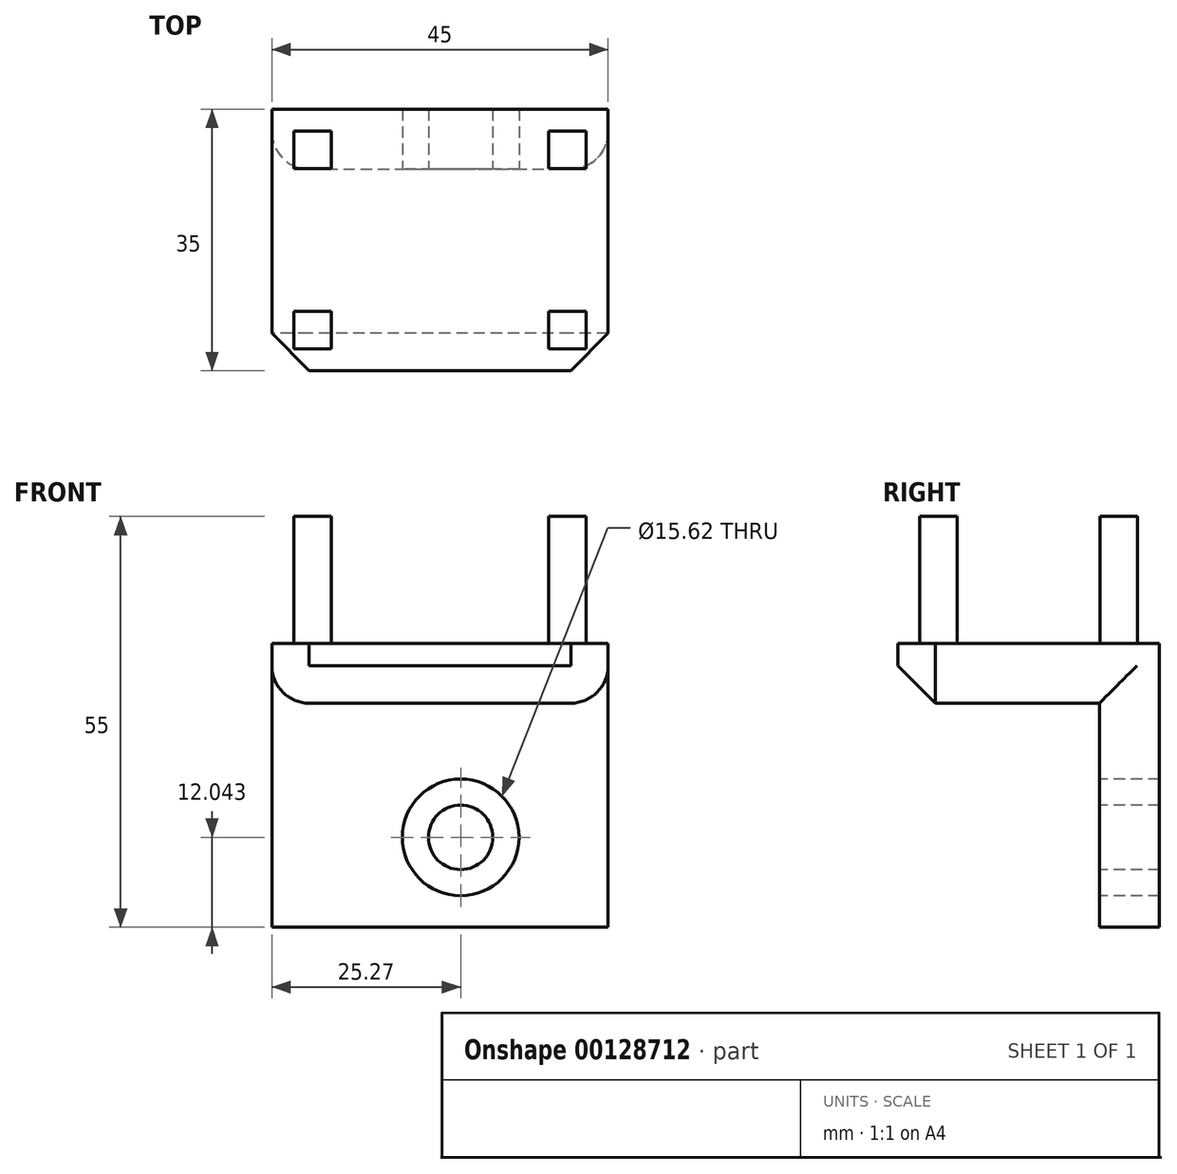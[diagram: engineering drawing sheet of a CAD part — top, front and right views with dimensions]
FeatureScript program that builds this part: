
annotation { "Feature Type Name" : "Feature", "Feature Type Description" : "" }
export const myFeature = defineFeature(function(context is Context, id is Id, definition is map)
    precondition{}
    {
        {
            var Q0;
            Q0=qCreatedBy(makeId("Top.planeOp"),FACE);
            var sketch = newSketch(context, id + "F0", { "sketchPlane" : qUnion([Q0])});
            skLineSegment(sketch, "E0.bottom", {"start": v(-22.5, -17.5) * mm, "end": v(22.5, -17.5) * mm});
            skLineSegment(sketch, "E0.top", {"start": v(-22.5, 17.5) * mm, "end": v(22.5, 17.5) * mm});
            skLineSegment(sketch, "E0.left", {"start": v(-22.5, -17.5) * mm, "end": v(-22.5, 17.5) * mm});
            skLineSegment(sketch, "E0.right", {"start": v(22.5, -17.5) * mm, "end": v(22.5, 17.5) * mm});
            skPoint(sketch, "E0.middle", {"position": v(0, 0) * mm});
            skLineSegment(sketch, "E1.top", {"start": v(-22.5, 9.49) * mm, "end": v(22.5, 9.49) * mm});
            skLineSegment(sketch, "E1.left", {"start": v(-22.5, 17.5) * mm, "end": v(-22.5, 9.49) * mm});
            skLineSegment(sketch, "E1.right", {"start": v(22.5, 17.5) * mm, "end": v(22.5, 9.49) * mm});
            skLineSegment(sketch, "E2.bottom", {"start": v(14.55, -9.55) * mm, "end": v(19.55, -9.55) * mm});
            skLineSegment(sketch, "E2.top", {"start": v(14.55, -14.55) * mm, "end": v(19.55, -14.55) * mm});
            skLineSegment(sketch, "E2.left", {"start": v(14.55, -9.55) * mm, "end": v(14.55, -14.55) * mm});
            skLineSegment(sketch, "E2.right", {"start": v(19.55, -9.55) * mm, "end": v(19.55, -14.55) * mm});
            skLineSegment(sketch, "E3.MirrorCS", {"start": v(19.55, 9.55) * mm, "end": v(19.55, 14.55) * mm});
            skLineSegment(sketch, "E4.MirrorCS", {"start": v(14.55, 9.55) * mm, "end": v(14.55, 14.55) * mm});
            skLineSegment(sketch, "E5.MirrorCS", {"start": v(14.55, 14.55) * mm, "end": v(19.55, 14.55) * mm});
            skLineSegment(sketch, "E6.MirrorCS", {"start": v(14.55, 9.55) * mm, "end": v(19.55, 9.55) * mm});
            skLineSegment(sketch, "E7.MirrorCS", {"start": v(-19.55, 9.55) * mm, "end": v(-19.55, 14.55) * mm});
            skLineSegment(sketch, "E8.MirrorCS", {"start": v(-19.55, -9.55) * mm, "end": v(-19.55, -14.55) * mm});
            skLineSegment(sketch, "E9.MirrorCS", {"start": v(-14.55, -9.55) * mm, "end": v(-14.55, -14.55) * mm});
            skLineSegment(sketch, "E10.MirrorCS", {"start": v(-14.55, -14.55) * mm, "end": v(-19.55, -14.55) * mm});
            skLineSegment(sketch, "E11.MirrorCS", {"start": v(-14.55, 9.55) * mm, "end": v(-14.55, 14.55) * mm});
            skLineSegment(sketch, "E12.MirrorCS", {"start": v(-14.55, -9.55) * mm, "end": v(-19.55, -9.55) * mm});
            skLineSegment(sketch, "E13.MirrorCS", {"start": v(-14.55, 9.55) * mm, "end": v(-19.55, 9.55) * mm});
            skLineSegment(sketch, "E14.MirrorCS", {"start": v(-14.55, 14.55) * mm, "end": v(-19.55, 14.55) * mm});
            skSolve(sketch);
        }
        {
            var Q0;
            Q0=makeQuery(id+"F0.imprint","IMPRINT",FACE,{"disambiguationData":[TD([[makeQuery(id+"F0.imprint","IMPRINT",EDGE,{"derivedFrom":sQuery(id+"F0.wireOp",EDGE,"E7.MirrorCS")}),-1.0]])]});
            var Q1;
            Q1=makeQuery(id+"F0.imprint","IMPRINT",FACE,{"disambiguationData":[TD([[makeQuery(id+"F0.imprint","IMPRINT",EDGE,{"derivedFrom":sQuery(id+"F0.wireOp",EDGE,"E8.MirrorCS")}),1.0]])]});
            var Q2;
            Q2=makeQuery(id+"F0.imprint","IMPRINT",FACE,{"disambiguationData":[TD([[makeQuery(id+"F0.imprint","IMPRINT",EDGE,{"derivedFrom":sQuery(id+"F0.wireOp",EDGE,"E2.bottom")}),-1.0]])]});
            var Q3;
            Q3=makeQuery(id+"F0.imprint","IMPRINT",FACE,{"disambiguationData":[TD([[makeQuery(id+"F0.imprint","IMPRINT",EDGE,{"derivedFrom":sQuery(id+"F0.wireOp",EDGE,"E3.MirrorCS")}),1.0]])]});
            var Q4;
            Q4=makeQuery(id+"F0.imprint","IMPRINT",FACE,{"disambiguationData":[TD([[makeQuery(id+"F0.imprint","IMPRINT",EDGE,{"derivedFrom":sQuery(id+"F0.wireOp",EDGE,"E0.bottom")}),1.0]])]});
            var Q5;
            Q5=makeQuery(id+"F0.imprint","IMPRINT",FACE,{"disambiguationData":[TD([[makeQuery(id+"F0.imprint","IMPRINT",EDGE,{"derivedFrom":sQuery(id+"F0.wireOp",EDGE,"E0.top")}),-1.0]])]});
            extrude(context, id + "F1", {"entities" : qUnion([Q0, Q1, Q2, Q3, Q4, Q5]), "depth" : 8 * mm});
        }
        {
            var Q0;
            Q0=makeQuery(id+"F0.imprint","IMPRINT",FACE,{"disambiguationData":[TD([[makeQuery(id+"F0.imprint","IMPRINT",EDGE,{"derivedFrom":sQuery(id+"F0.wireOp",EDGE,"E8.MirrorCS")}),1.0]])]});
            var Q1;
            Q1=makeQuery(id+"F0.imprint","IMPRINT",FACE,{"disambiguationData":[TD([[makeQuery(id+"F0.imprint","IMPRINT",EDGE,{"derivedFrom":sQuery(id+"F0.wireOp",EDGE,"E7.MirrorCS")}),-1.0]])]});
            var Q2;
            Q2=makeQuery(id+"F0.imprint","IMPRINT",FACE,{"disambiguationData":[TD([[makeQuery(id+"F0.imprint","IMPRINT",EDGE,{"derivedFrom":sQuery(id+"F0.wireOp",EDGE,"E2.bottom")}),-1.0]])]});
            var Q3;
            Q3=makeQuery(id+"F0.imprint","IMPRINT",FACE,{"disambiguationData":[TD([[makeQuery(id+"F0.imprint","IMPRINT",EDGE,{"derivedFrom":sQuery(id+"F0.wireOp",EDGE,"E3.MirrorCS")}),1.0]])]});
            extrude(context, id + "F2", {"entities" : qUnion([Q0, Q1, Q2, Q3]), "operationType" : NewBodyOperationType.ADD, "depth" : 25 * mm});
        }
        {
            var Q0;
            Q0=makeQuery(id+"F0.imprint","IMPRINT",FACE,{"disambiguationData":[TD([[makeQuery(id+"F0.imprint","IMPRINT",EDGE,{"derivedFrom":sQuery(id+"F0.wireOp",EDGE,"E0.top")}),-1.0]])]});
            var Q1;
            Q1=makeQuery(id+"F0.imprint","IMPRINT",FACE,{"disambiguationData":[TD([[makeQuery(id+"F0.imprint","IMPRINT",EDGE,{"derivedFrom":sQuery(id+"F0.wireOp",EDGE,"E3.MirrorCS")}),1.0]])]});
            var Q2;
            Q2=makeQuery(id+"F0.imprint","IMPRINT",FACE,{"disambiguationData":[TD([[makeQuery(id+"F0.imprint","IMPRINT",EDGE,{"derivedFrom":sQuery(id+"F0.wireOp",EDGE,"E7.MirrorCS")}),-1.0]])]});
            extrude(context, id + "F3", {"entities" : qUnion([Q0, Q1, Q2]), "operationType" : NewBodyOperationType.ADD, "oppositeDirection" : true, "depth" : 30 * mm});
        }
        {
            var Q0;
            Q0=makeQuery(id+"F3.opExtrude","CAP_EDGE",EDGE,{"disambiguationData":[OSD([sQuery(id+"F0.wireOp",EDGE,"E1.right")])],"isStart":false});
            var Q1;
            Q1=makeQuery(id+"F3.opExtrude","CAP_EDGE",EDGE,{"disambiguationData":[OSD([sQuery(id+"F0.wireOp",EDGE,"E1.left")])],"isStart":false});
            var Q2;
            Q2=makeQuery(id+"F3.opExtrude","SWEPT_EDGE",EDGE,{"disambiguationData":[OSD([sQuery(id+"F0.wireOp",EDGE,"E0.left"),sQuery(id+"F0.wireOp",EDGE,"E1.top"),sQuery(id+"F0.wireOp",EDGE,"E1.left")])]});
            var Q3;
            Q3=makeQuery(id+"F3.opExtrude","SWEPT_EDGE",EDGE,{"disambiguationData":[OSD([sQuery(id+"F0.wireOp",EDGE,"E0.right"),sQuery(id+"F0.wireOp",EDGE,"E1.top"),sQuery(id+"F0.wireOp",EDGE,"E1.right")])]});
            fillet(context, id + "F4", {"entities" : qUnion([Q0, Q1, Q2, Q3]), "radius" : 5 * mm, "tangentPropagation" : true, "allowEdgeOverflow" : false});
        }
        {
            var Q0;
            Q0=makeQuery(id+"F1.opExtrude","CAP_EDGE",EDGE,{"disambiguationData":[OSD([sQuery(id+"F0.wireOp",EDGE,"E0.right"),sQuery(id+"F0.wireOp",EDGE,"E1.right")])],"isStart":true});
            var Q1;
            Q1=makeQuery(id+"F1.opExtrude","CAP_EDGE",EDGE,{"disambiguationData":[OSD([sQuery(id+"F0.wireOp",EDGE,"E0.left"),sQuery(id+"F0.wireOp",EDGE,"E1.left")])],"isStart":true});
            fillet(context, id + "F5", {"entities" : qUnion([Q0, Q1]), "radius" : 5 * mm, "tangentPropagation" : true, "allowEdgeOverflow" : false});
        }
        {
            var Q0;
            Q0=makeQuery(id+"F1.opExtrude","CAP_EDGE",EDGE,{"disambiguationData":[OSD([sQuery(id+"F0.wireOp",EDGE,"E0.bottom")])],"isStart":true});
            chamfer(context, id + "F6", {"entities" : qUnion([Q0]), "width" : 5 * mm, "tangentPropagation" : true});
        }
        {
            var Q0;
            Q0=makeQuery(id+"F3.opExtrude","SWEPT_FACE",FACE,{"disambiguationData":[OSD([sQuery(id+"F0.wireOp",EDGE,"E1.top")])]});
            var sketch = newSketch(context, id + "F7", { "sketchPlane" : qUnion([Q0])});
            skCircle(sketch, "E15", {"center": v(2.77, -17.96) * mm, "radius": 7.81 * mm});
            skCircle(sketch, "E16", {"center": v(2.77, -17.96) * mm, "radius": 4.31 * mm});
            skSolve(sketch);
        }
        {
            var Q0;
            Q0 = qSketchRegion(id + "F7", true);
            extrude(context, id + "F8", {"entities" : qUnion([Q0]), "operationType" : NewBodyOperationType.REMOVE, "oppositeDirection" : true, "depth" : 25 * mm});
        }
    });
